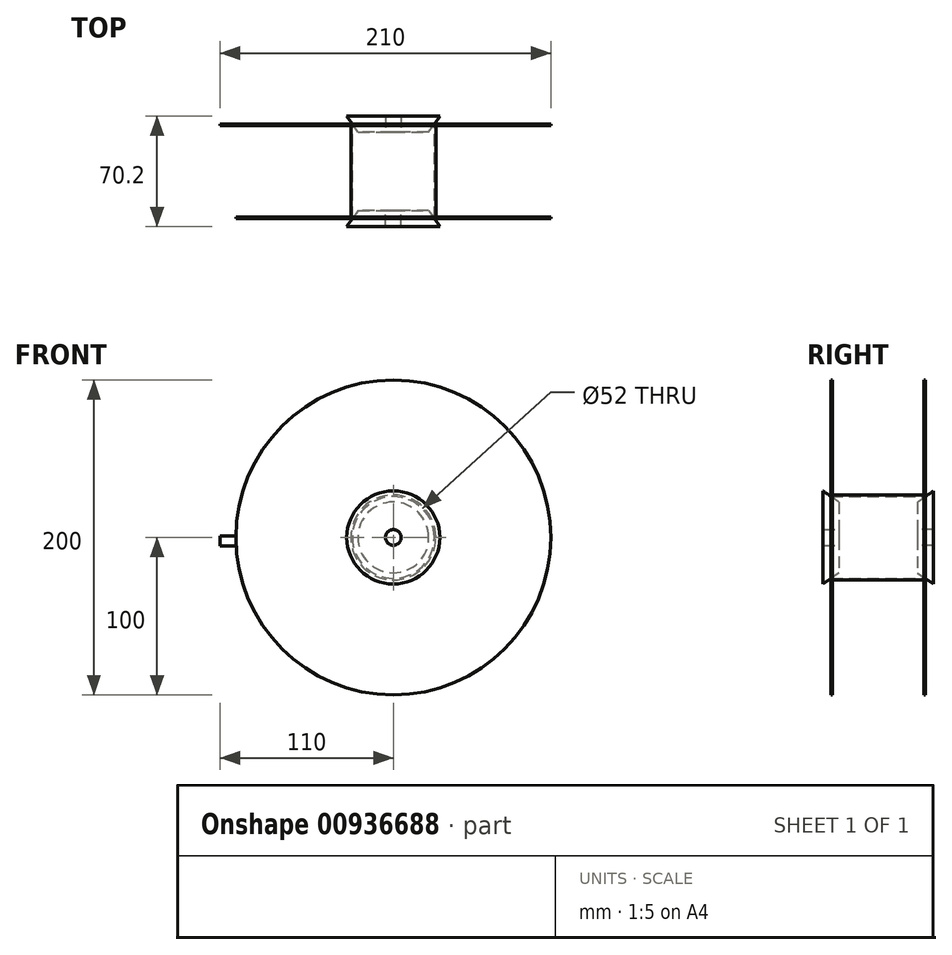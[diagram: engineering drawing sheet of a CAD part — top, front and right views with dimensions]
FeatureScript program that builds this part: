
annotation { "Feature Type Name" : "Feature", "Feature Type Description" : "" }
export const myFeature = defineFeature(function(context is Context, id is Id, definition is map)
    precondition{}
    {
        {
            var Q0;
            Q0=qCreatedBy(makeId("Right.planeOp"),FACE);
            var sketch = newSketch(context, id + "F0", { "sketchPlane" : qUnion([Q0])});
            skLineSegment(sketch, "E0", {"start": v(-60, 74) * mm, "end": v(-60, 0) * mm});
            skLineSegment(sketch, "E1", {"start": v(-60, 0) * mm, "end": v(0, 0) * mm});
            skLineSegment(sketch, "E2", {"start": v(0, -26) * mm, "end": v(-60, -26) * mm, "construction": true});
            skLineSegment(sketch, "E3", {"start": v(0, 0) * mm, "end": v(0, 74) * mm});
            skLineSegment(sketch, "E4", {"start": v(-55, -3.5) * mm, "end": v(-65.1, 3.57) * mm});
            skLineSegment(sketch, "E5", {"start": v(-5, -3.5) * mm, "end": v(5.1, 3.57) * mm});
            skLineSegment(sketch, "E6", {"start": v(5.1, 3.57) * mm, "end": v(5.1, -21) * mm});
            skLineSegment(sketch, "E7", {"start": v(-5, -3.5) * mm, "end": v(-5, -21) * mm});
            skLineSegment(sketch, "E8", {"start": v(-5, -21) * mm, "end": v(5.1, -21) * mm});
            skLineSegment(sketch, "E9", {"start": v(-55, -3.5) * mm, "end": v(-55, -21) * mm});
            skLineSegment(sketch, "E10", {"start": v(-65.1, 3.57) * mm, "end": v(-65.1, -21) * mm});
            skLineSegment(sketch, "E11", {"start": v(-65.1, -21) * mm, "end": v(-55, -21) * mm});
            skLineSegment(sketch, "E12.0", {"start": v(-1, 1) * mm, "end": v(-1, 74) * mm});
            skLineSegment(sketch, "E12.1", {"start": v(-59, 1) * mm, "end": v(-1, 1) * mm});
            skLineSegment(sketch, "E12.2", {"start": v(-59, 74) * mm, "end": v(-59, 1) * mm});
            skLineSegment(sketch, "E13", {"start": v(-60, 74) * mm, "end": v(-59, 74) * mm});
            skLineSegment(sketch, "E14", {"start": v(-1, 74) * mm, "end": v(0, 74) * mm});
            skLineSegment(sketch, "E15.0", {"start": v(-64.1, 1.65) * mm, "end": v(-64.1, -20) * mm});
            skLineSegment(sketch, "E15.1", {"start": v(-56, -4.02) * mm, "end": v(-64.1, 1.65) * mm});
            skLineSegment(sketch, "E15.2", {"start": v(-56, -4.02) * mm, "end": v(-56, -20) * mm});
            skLineSegment(sketch, "E15.3", {"start": v(-64.1, -20) * mm, "end": v(-56, -20) * mm});
            skLineSegment(sketch, "E16.0", {"start": v(-4, -4.02) * mm, "end": v(-4, -20) * mm});
            skLineSegment(sketch, "E16.1", {"start": v(-4, -4.02) * mm, "end": v(4.1, 1.65) * mm});
            skLineSegment(sketch, "E16.2", {"start": v(4.1, 1.65) * mm, "end": v(4.1, -20) * mm});
            skLineSegment(sketch, "E16.3", {"start": v(-4, -20) * mm, "end": v(4.1, -20) * mm});
            skSolve(sketch);
        }
        {
            var Q0;
            Q0=makeQuery(id+"F0.imprint","IMPRINT",FACE,{"disambiguationData":[TD([[makeQuery(id+"F0.imprint","IMPRINT",EDGE,{"derivedFrom":sQuery(id+"F0.wireOp",EDGE,"E0")}),1.0]])]});
            var Q1;
            Q1=sQuery(id+"F0.wireOp",EDGE,"E0");
            var Q2;
            Q2=sQuery(id+"F0.wireOp",EDGE,"E1");
            var Q3;
            Q3=sQuery(id+"F0.wireOp",EDGE,"E3");
            var Q4;
            Q4=sQuery(id+"F0.wireOp",EDGE,"E12.1");
            var Q5;
            Q5=sQuery(id+"F0.wireOp",EDGE,"E12.2");
            var Q6;
            Q6=sQuery(id+"F0.wireOp",EDGE,"E12.0");
            var Q7;
            Q7=sQuery(id+"F0.wireOp",EDGE,"E13");
            var Q8;
            Q8=sQuery(id+"F0.wireOp",EDGE,"E14");
            var Q9;
            Q9=sQuery(id+"F0.wireOp",EDGE,"E2");
            revolve(context, id + "F1", {"surfaceOperationType" : NewSurfaceOperationType.NEW, "entities" : qUnion([Q0]), "surfaceEntities" : qUnion([Q1, Q2, Q3, Q4, Q5, Q6, Q7, Q8]), "axis" : qUnion([Q9]), "revolveType" : RevolveType.FULL});
        }
        {
            var Q0;
            Q0=makeQuery(id+"F0.imprint","IMPRINT",FACE,{"disambiguationData":[TD([[makeQuery(id+"F0.imprint","IMPRINT",EDGE,{"derivedFrom":sQuery(id+"F0.wireOp",EDGE,"E15.0")}),1.0]])]});
            var Q1;
            {var subQ1=sQuery(id+"F0.wireOp",EDGE,"E9");Q1=makeQuery(id+"F0.imprint","IMPRINT",FACE,{"disambiguationData":[TD([[makeQuery(id+"F0.imprint","IMPRINT",EDGE,{"derivedFrom":subQ1}),-1.0]])]});}
            var Q2;
            {var subQ1=sQuery(id+"F0.wireOp",EDGE,"E6");Q2=makeQuery(id+"F0.imprint","IMPRINT",FACE,{"disambiguationData":[TD([[makeQuery(id+"F0.imprint","IMPRINT",EDGE,{"derivedFrom":subQ1}),-1.0]])]});}
            var Q3;
            Q3=makeQuery(id+"F0.imprint","IMPRINT",FACE,{"disambiguationData":[TD([[makeQuery(id+"F0.imprint","IMPRINT",EDGE,{"derivedFrom":sQuery(id+"F0.wireOp",EDGE,"E16.0")}),1.0]])]});
            var Q4;
            Q4=sQuery(id+"F0.wireOp",EDGE,"E6");
            var Q5;
            Q5=sQuery(id+"F0.wireOp",EDGE,"E5");
            var Q6;
            Q6=sQuery(id+"F0.wireOp",EDGE,"E7");
            var Q7;
            Q7=sQuery(id+"F0.wireOp",EDGE,"E8");
            var Q8;
            Q8=sQuery(id+"F0.wireOp",EDGE,"E11");
            var Q9;
            Q9=sQuery(id+"F0.wireOp",EDGE,"E9");
            var Q10;
            Q10=sQuery(id+"F0.wireOp",EDGE,"E4");
            var Q11;
            Q11=sQuery(id+"F0.wireOp",EDGE,"E10");
            var Q12;
            Q12=sQuery(id+"F0.wireOp",EDGE,"E2");
            revolve(context, id + "F2", {"surfaceOperationType" : NewSurfaceOperationType.NEW, "entities" : qUnion([Q0, Q1, Q2, Q3]), "surfaceEntities" : qUnion([Q4, Q5, Q6, Q7, Q8, Q9, Q10, Q11]), "axis" : qUnion([Q12]), "revolveType" : RevolveType.FULL});
        }
        {
            var Q0;
            Q0=makeQuery(id+"F1.opRevolve","SWEPT_FACE",FACE,{"disambiguationData":[OSD([sQuery(id+"F0.wireOp",EDGE,"E3")])]});
            var sketch = newSketch(context, id + "F3", { "sketchPlane" : qUnion([Q0])});
            skLineSegment(sketch, "E17", {"start": v(99.86, -31.29) * mm, "end": v(110, -31.29) * mm});
            skLineSegment(sketch, "E18", {"start": v(110, -31.29) * mm, "end": v(110, -25.16) * mm});
            skLineSegment(sketch, "E19", {"start": v(110, -25.16) * mm, "end": v(100, -25.16) * mm});
            skSolve(sketch);
        }
        {
            var Q0;
            {var subQ0=sQuery(id+"F3.wireOp",EDGE,"E17");Q0=makeQuery(id+"F3.imprint","IMPRINT",FACE,{"disambiguationData":[TD([[makeQuery(id+"F3.imprint","IMPRINT",EDGE,{"derivedFrom":subQ0}),1.0]])]});}
            extrude(context, id + "F4", {"entities" : qUnion([Q0]), "operationType" : NewBodyOperationType.ADD, "oppositeDirection" : true, "depth" : 1 * mm, "offsetDistance" : 25 * mm});
        }
    });
